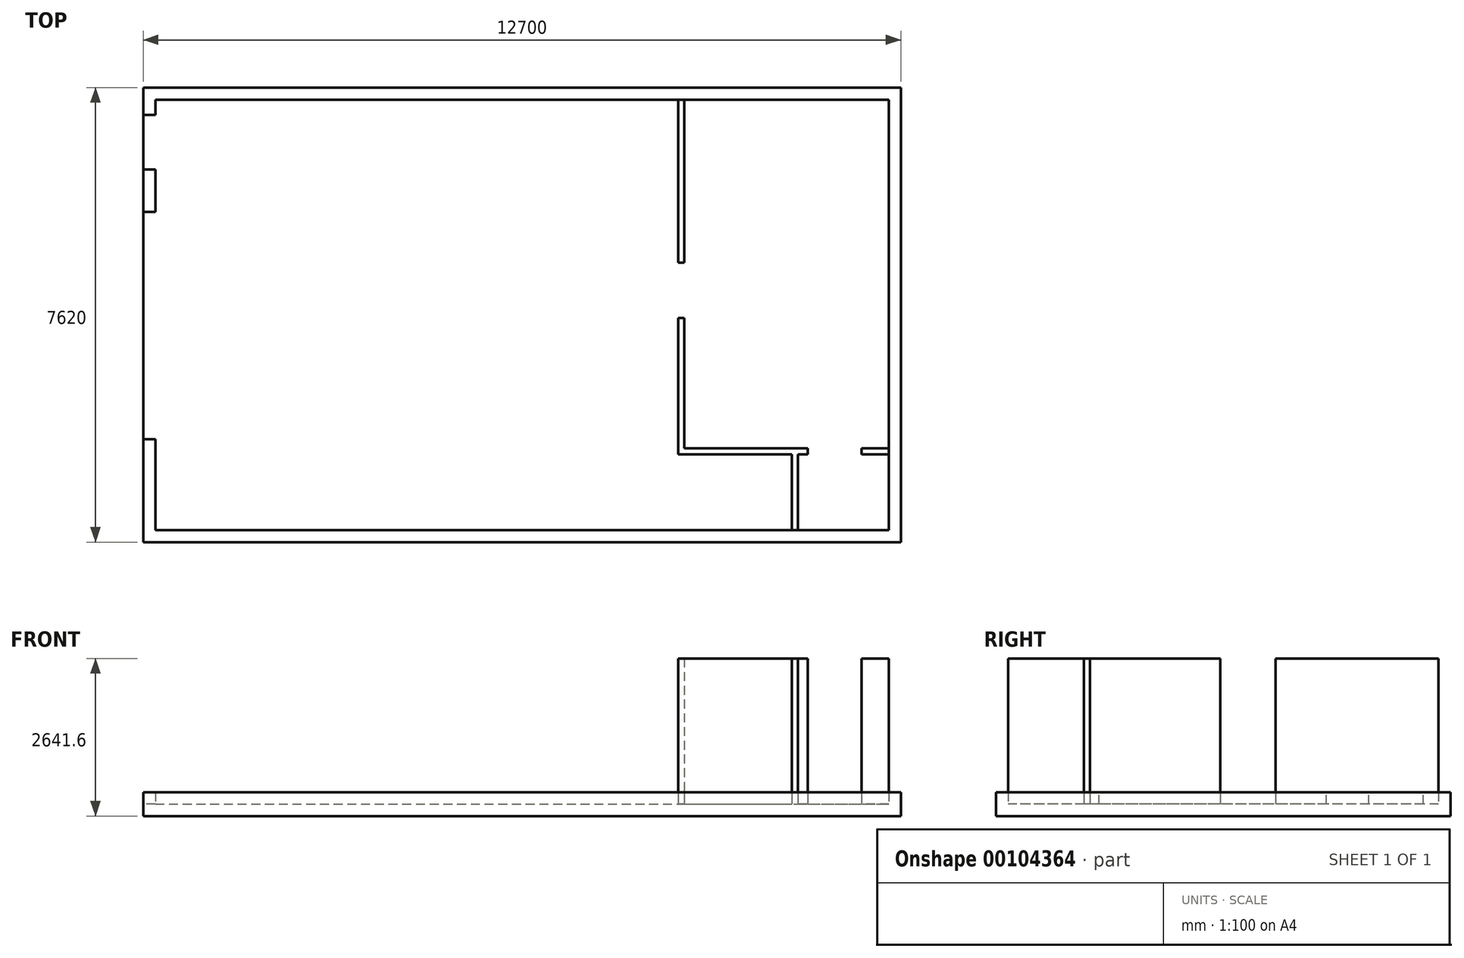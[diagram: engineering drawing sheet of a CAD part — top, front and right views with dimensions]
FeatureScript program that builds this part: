
annotation { "Feature Type Name" : "Feature", "Feature Type Description" : "" }
export const myFeature = defineFeature(function(context is Context, id is Id, definition is map)
    precondition{}
    {
        {
            assignVariable(context, id + "F0", {"name" : "FloorThickness", "anyValue" : 203.2 * mm});
        }
        {
            assignVariable(context, id + "F1", {"name" : "BuildingHeight", "anyValue" : 192});
        }
        {
            assignVariable(context, id + "F2", {"name" : "OfficeWallHeight", "anyValue" : 2438.4 * mm});
        }
        {
            var Q0;
            Q0=qCreatedBy(makeId("Top.planeOp"),FACE);
            var sketch = newSketch(context, id + "F3", { "sketchPlane" : qUnion([Q0])});
            skLineSegment(sketch, "E0.bottom", {"start": v(-6348.17, 3963.91) * mm, "end": v(6351.83, 3963.91) * mm});
            skLineSegment(sketch, "E0.top", {"start": v(-6348.17, -3656.09) * mm, "end": v(6351.83, -3656.09) * mm});
            skLineSegment(sketch, "E0.left", {"start": v(-6348.17, 3963.91) * mm, "end": v(-6348.17, -3656.09) * mm});
            skLineSegment(sketch, "E0.right", {"start": v(6351.83, 3963.91) * mm, "end": v(6351.83, -3656.09) * mm});
            skSolve(sketch);
        }
        {
            var Q0;
            Q0=makeQuery(id+"F3.imprint","IMPRINT",FACE,{"disambiguationData":[TD([[makeQuery(id+"F3.imprint","IMPRINT",EDGE,{"derivedFrom":sQuery(id+"F3.wireOp",EDGE,"E0.bottom")}),-1.0]])]});
            extrude(context, id + "F4", {"entities" : qUnion([Q0]), "depth" : getVariable(context, 'FloorThickness')});
        }
        {
            var Q0;
            Q0=makeQuery(id+"F4.opExtrude","CAP_FACE",FACE,{"disambiguationData":[OSD([sQuery(id+"F3.wireOp",EDGE,"E0.bottom"),sQuery(id+"F3.wireOp",EDGE,"E0.top"),sQuery(id+"F3.wireOp",EDGE,"E0.left"),sQuery(id+"F3.wireOp",EDGE,"E0.right")])],"isStart":false});
            var sketch = newSketch(context, id + "F5", { "sketchPlane" : qUnion([Q0])});
            skLineSegment(sketch, "E1.bottom", {"start": v(-6144.97, 3760.71) * mm, "end": v(6148.63, 3760.71) * mm});
            skLineSegment(sketch, "E1.top", {"start": v(-6144.97, -3452.89) * mm, "end": v(6148.63, -3452.89) * mm});
            skLineSegment(sketch, "E1.left", {"start": v(-6144.97, 3760.71) * mm, "end": v(-6144.97, -3452.89) * mm});
            skLineSegment(sketch, "E1.right", {"start": v(6148.63, 3760.71) * mm, "end": v(6148.63, -3452.89) * mm});
            skLineSegment(sketch, "E2.bottom", {"start": v(-6348.17, 3963.91) * mm, "end": v(6351.83, 3963.91) * mm});
            skLineSegment(sketch, "E2.top", {"start": v(-6348.17, -3656.09) * mm, "end": v(6351.83, -3656.09) * mm});
            skLineSegment(sketch, "E2.left", {"start": v(-6348.17, 3963.91) * mm, "end": v(-6348.17, -3656.09) * mm});
            skLineSegment(sketch, "E2.right", {"start": v(6351.83, 3963.91) * mm, "end": v(6351.83, -3656.09) * mm});
            skSolve(sketch);
        }
        {
            var Q0;
            Q0 = qSketchRegion(id + "F5", true);
            extrude(context, id + "F6", {"entities" : qUnion([Q0]), "operationType" : NewBodyOperationType.ADD, "depth" : (getVariable(context, 'BuildingHeight')) * mm});
        }
        {
            var Q0;
            Q0=makeQuery(id+"F6.boolean.opBoolean","MERGE",FACE,{"derivedFrom":[makeQuery(id+"F4.opExtrude","SWEPT_FACE",FACE,{"disambiguationData":[OSD([sQuery(id+"F3.wireOp",EDGE,"E0.left")])]}),makeQuery(id+"F6.opExtrude","SWEPT_FACE",FACE,{"disambiguationData":[OSD([sQuery(id+"F5.wireOp",EDGE,"E2.left")])]})]});
            var sketch = newSketch(context, id + "F7", { "sketchPlane" : qUnion([Q0])});
            skLineSegment(sketch, "E3.bottom", {"start": v(-1881.11, 203.2) * mm, "end": v(1928.89, 203.2) * mm});
            skLineSegment(sketch, "E3.top", {"start": v(-1881.11, 4470.4) * mm, "end": v(1928.89, 4470.4) * mm});
            skLineSegment(sketch, "E3.left", {"start": v(-1881.11, 203.2) * mm, "end": v(-1881.11, 4470.4) * mm});
            skLineSegment(sketch, "E3.right", {"start": v(1928.89, 203.2) * mm, "end": v(1928.89, 4470.4) * mm});
            skLineSegment(sketch, "E4.bottom", {"start": v(-3506.71, 203.2) * mm, "end": v(-2592.31, 203.2) * mm});
            skLineSegment(sketch, "E4.top", {"start": v(-3506.71, 2235.2) * mm, "end": v(-2592.31, 2235.2) * mm});
            skLineSegment(sketch, "E4.left", {"start": v(-3506.71, 203.2) * mm, "end": v(-3506.71, 2235.2) * mm});
            skLineSegment(sketch, "E4.right", {"start": v(-2592.31, 203.2) * mm, "end": v(-2592.31, 2235.2) * mm});
            skSolve(sketch);
        }
        {
            var Q0;
            Q0=makeQuery(id+"F7.imprint","IMPRINT",FACE,{"disambiguationData":[TD([[makeQuery(id+"F7.imprint","IMPRINT",EDGE,{"derivedFrom":sQuery(id+"F7.wireOp",EDGE,"E3.bottom")}),1.0]])]});
            var Q1;
            Q1=makeQuery(id+"F7.imprint","IMPRINT",FACE,{"disambiguationData":[TD([[makeQuery(id+"F7.imprint","IMPRINT",EDGE,{"derivedFrom":sQuery(id+"F7.wireOp",EDGE,"E4.bottom")}),1.0]])]});
            extrude(context, id + "F8", {"entities" : qUnion([Q0, Q1]), "operationType" : NewBodyOperationType.REMOVE, "endBound" : BoundingType.UP_TO_NEXT, "oppositeDirection" : true, "depth" : 1514.4 * mm});
        }
        {
            var Q0;
            Q0=makeQuery(id+"F8.boolean.opBoolean","MERGE",FACE,{"derivedFrom":[makeQuery(id+"F4.opExtrude","CAP_FACE",FACE,{"disambiguationData":[OSD([sQuery(id+"F3.wireOp",EDGE,"E0.bottom"),sQuery(id+"F3.wireOp",EDGE,"E0.top"),sQuery(id+"F3.wireOp",EDGE,"E0.left"),sQuery(id+"F3.wireOp",EDGE,"E0.right")])],"isStart":false}),makeQuery(id+"F8.opExtrude","SWEPT_FACE",FACE,{"disambiguationData":[OSD([sQuery(id+"F7.wireOp",EDGE,"E3.bottom")])]}),makeQuery(id+"F8.opExtrude","SWEPT_FACE",FACE,{"disambiguationData":[OSD([sQuery(id+"F7.wireOp",EDGE,"E4.bottom")])]})]});
            var sketch = newSketch(context, id + "F9", { "sketchPlane" : qUnion([Q0])});
            skLineSegment(sketch, "E5", {"start": v(6148.63, 3760.71) * mm, "end": v(2618.03, 3760.71) * mm});
            skLineSegment(sketch, "E6", {"start": v(2618.03, 3760.71) * mm, "end": v(2618.03, -2182.89) * mm});
            skLineSegment(sketch, "E7", {"start": v(2618.03, -2182.89) * mm, "end": v(4523.03, -2182.89) * mm});
            skLineSegment(sketch, "E8", {"start": v(4523.03, -2182.89) * mm, "end": v(4523.03, -3452.89) * mm});
            skLineSegment(sketch, "E9", {"start": v(4523.03, -3452.89) * mm, "end": v(6148.63, -3452.89) * mm});
            skLineSegment(sketch, "E10", {"start": v(6148.63, -3452.89) * mm, "end": v(6148.63, 3760.71) * mm});
            skLineSegment(sketch, "E11", {"start": v(2719.63, 3760.71) * mm, "end": v(2719.63, -2081.29) * mm});
            skLineSegment(sketch, "E12", {"start": v(2719.63, -2081.29) * mm, "end": v(4624.63, -2081.29) * mm});
            skLineSegment(sketch, "E13", {"start": v(4624.63, -2182.89) * mm, "end": v(4624.63, -3452.89) * mm});
            skLineSegment(sketch, "E14", {"start": v(4624.63, -2081.29) * mm, "end": v(4789.73, -2081.29) * mm});
            skLineSegment(sketch, "E15", {"start": v(4789.73, -2081.29) * mm, "end": v(4789.73, -2182.89) * mm});
            skLineSegment(sketch, "E16", {"start": v(4789.73, -2182.89) * mm, "end": v(4624.63, -2182.89) * mm});
            skLineSegment(sketch, "E17.bottom", {"start": v(6148.63, -2081.29) * mm, "end": v(5691.43, -2081.29) * mm});
            skLineSegment(sketch, "E17.top", {"start": v(6148.63, -2182.89) * mm, "end": v(5691.43, -2182.89) * mm});
            skLineSegment(sketch, "E17.left", {"start": v(6148.63, -2081.29) * mm, "end": v(6148.63, -2182.89) * mm});
            skLineSegment(sketch, "E17.right", {"start": v(5691.43, -2081.29) * mm, "end": v(5691.43, -2182.89) * mm});
            skSolve(sketch);
        }
        {
            var Q0;
            {var subQ1=sQuery(id+"F9.wireOp",EDGE,"E6");Q0=makeQuery(id+"F9.imprint","IMPRINT",FACE,{"disambiguationData":[TD([[makeQuery(id+"F9.imprint","IMPRINT",EDGE,{"derivedFrom":subQ1}),1.0]])]});}
            var Q1;
            Q1=makeQuery(id+"F9.imprint","IMPRINT",FACE,{"disambiguationData":[TD([[makeQuery(id+"F9.imprint","IMPRINT",EDGE,{"derivedFrom":sQuery(id+"F9.wireOp",EDGE,"E17.bottom")}),1.0]])]});
            extrude(context, id + "F10", {"entities" : qUnion([Q0, Q1]), "operationType" : NewBodyOperationType.ADD, "depth" : getVariable(context, 'OfficeWallHeight')});
        }
        {
            var Q0;
            Q0=makeQuery(id+"F10.opExtrude","SWEPT_FACE",FACE,{"disambiguationData":[OSD([sQuery(id+"F9.wireOp",EDGE,"E6")])]});
            var sketch = newSketch(context, id + "F11", { "sketchPlane" : qUnion([Q0])});
            skLineSegment(sketch, "E18.bottom", {"start": v(-1025.13, 2641.6) * mm, "end": v(-103.11, 2641.6) * mm});
            skLineSegment(sketch, "E18.top", {"start": v(-1025.13, 203.2) * mm, "end": v(-103.11, 203.2) * mm});
            skLineSegment(sketch, "E18.left", {"start": v(-1025.13, 2641.6) * mm, "end": v(-1025.13, 203.2) * mm});
            skLineSegment(sketch, "E18.right", {"start": v(-103.11, 2641.6) * mm, "end": v(-103.11, 203.2) * mm});
            skSolve(sketch);
        }
        {
            var Q0;
            Q0 = qSketchRegion(id + "F11", true);
            extrude(context, id + "F12", {"entities" : qUnion([Q0]), "operationType" : NewBodyOperationType.REMOVE, "endBound" : BoundingType.UP_TO_NEXT, "oppositeDirection" : true, "depth" : 25.4 * mm});
        }
    });
